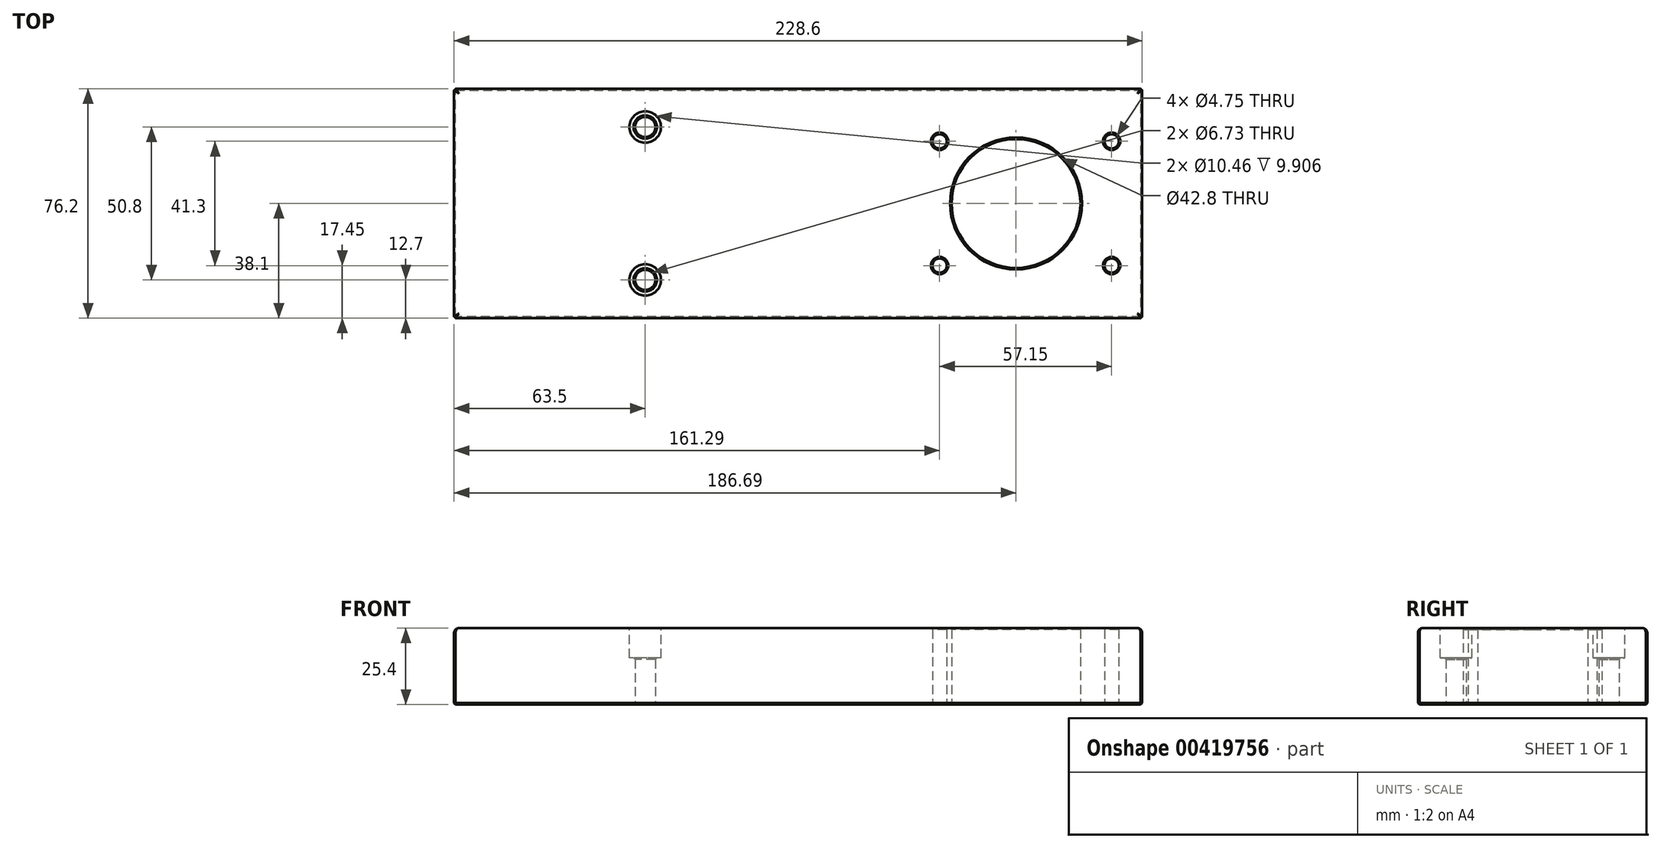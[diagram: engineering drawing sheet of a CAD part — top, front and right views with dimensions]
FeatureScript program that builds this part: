
annotation { "Feature Type Name" : "Feature", "Feature Type Description" : "" }
export const myFeature = defineFeature(function(context is Context, id is Id, definition is map)
    precondition{}
    {
        {
            var Q0;
            Q0=qCreatedBy(makeId("Top.planeOp"),FACE);
            var sketch = newSketch(context, id + "F0", { "sketchPlane" : qUnion([Q0])});
            skLineSegment(sketch, "E0.bottom", {"start": v(-114.3, -38.1) * mm, "end": v(114.3, -38.1) * mm});
            skLineSegment(sketch, "E0.top", {"start": v(-114.3, 38.1) * mm, "end": v(114.3, 38.1) * mm});
            skLineSegment(sketch, "E0.left", {"start": v(-114.3, -38.1) * mm, "end": v(-114.3, 38.1) * mm});
            skLineSegment(sketch, "E0.right", {"start": v(114.3, -38.1) * mm, "end": v(114.3, 38.1) * mm});
            skPoint(sketch, "E0.middle", {"position": v(0, 0) * mm});
            skLineSegment(sketch, "E1", {"start": v(0, 0) * mm, "end": v(0, 0) * mm});
            skPoint(sketch, "E1.endSnap0", {"position": v(0, -38.1) * mm});
            skLineSegment(sketch, "E2", {"start": v(0, 0) * mm, "end": v(-123.94, 0) * mm, "construction": true});
            skLineSegment(sketch, "E3", {"start": v(72.4, 38.1) * mm, "end": v(72.4, -38.1) * mm, "construction": true});
            skCircle(sketch, "E4", {"center": v(72.4, 0) * mm, "radius": 21.4 * mm});
            skCircle(sketch, "E5", {"center": v(104.14, 20.65) * mm, "radius": 2.37 * mm});
            skLineSegment(sketch, "E6", {"start": v(-47.63, 38.1) * mm, "end": v(-47.62, -38.1) * mm, "construction": true});
            skCircle(sketch, "E7", {"center": v(47, 20.65) * mm, "radius": 2.37 * mm});
            skCircle(sketch, "E8.MirrorC", {"center": v(47, -20.65) * mm, "radius": 2.37 * mm});
            skCircle(sketch, "E9.MirrorC", {"center": v(104.14, -20.65) * mm, "radius": 2.37 * mm});
            skLineSegment(sketch, "E10", {"start": v(-102.12, 25.4) * mm, "end": v(-23.36, 25.4) * mm, "construction": true});
            skLineSegment(sketch, "E11.MirrorCS", {"start": v(-102.12, -25.4) * mm, "end": v(-23.36, -25.4) * mm, "construction": true});
            skPoint(sketch, "E12", {"position": v(-47.63, 25.4) * mm});
            skPoint(sketch, "E13", {"position": v(-47.62, -25.4) * mm});
            skSolve(sketch);
        }
        {
            var Q0;
            Q0 = qSketchRegion(id + "F0", true);
            extrude(context, id + "F1", {"entities" : qUnion([Q0]), "depth" : 25.4 * mm});
        }
        {
            var Q0;
            Q0=qCreatedBy(makeId("Top.planeOp"),FACE);
            var sketch = newSketch(context, id + "F2", { "sketchPlane" : qUnion([Q0])});
            skLineSegment(sketch, "E14", {"start": v(-114.74, 25.4) * mm, "end": v(0, 25.4) * mm, "construction": true});
            skLineSegment(sketch, "E15", {"start": v(0, 0) * mm, "end": v(-152.98, 0) * mm, "construction": true});
            skLineSegment(sketch, "E16", {"start": v(-50.8, 25.4) * mm, "end": v(-50.8, 0) * mm, "construction": true});
            skCircle(sketch, "E17", {"center": v(-50.8, 25.4) * mm, "radius": 3.37 * mm});
            skLineSegment(sketch, "E18.MirrorCS", {"start": v(-114.74, -25.4) * mm, "end": v(0, -25.4) * mm, "construction": true});
            skLineSegment(sketch, "E19.MirrorCS", {"start": v(-50.8, -25.4) * mm, "end": v(-50.8, 0) * mm, "construction": true});
            skCircle(sketch, "E20.MirrorC", {"center": v(-50.8, -25.4) * mm, "radius": 3.37 * mm});
            skSolve(sketch);
        }
        {
            var Q0;
            Q0 = qSketchRegion(id + "F2", true);
            extrude(context, id + "F3", {"entities" : qUnion([Q0]), "operationType" : NewBodyOperationType.REMOVE, "depth" : 15.75 * mm});
        }
        {
            var Q0;
            Q0=makeQuery(id+"F1.opExtrude","CAP_FACE",FACE,{"disambiguationData":[OSD([sQuery(id+"F0.wireOp",EDGE,"E0.bottom"),sQuery(id+"F0.wireOp",EDGE,"E0.top"),sQuery(id+"F0.wireOp",EDGE,"E0.left"),sQuery(id+"F0.wireOp",EDGE,"E0.right"),sQuery(id+"F0.wireOp",EDGE,"E4"),sQuery(id+"F0.wireOp",EDGE,"E5"),sQuery(id+"F0.wireOp",EDGE,"E7"),sQuery(id+"F0.wireOp",EDGE,"E8.MirrorC"),sQuery(id+"F0.wireOp",EDGE,"E9.MirrorC")])],"isStart":false});
            var sketch = newSketch(context, id + "F4", { "sketchPlane" : qUnion([Q0])});
            skLineSegment(sketch, "E21", {"start": v(0, 25.4) * mm, "end": v(-89.53, 25.4) * mm, "construction": true});
            skLineSegment(sketch, "E22", {"start": v(0, 0) * mm, "end": v(-84.6, 0) * mm, "construction": true});
            skLineSegment(sketch, "E23", {"start": v(0, -25.4) * mm, "end": v(-84.6, -25.4) * mm, "construction": true});
            skLineSegment(sketch, "E24", {"start": v(-50.8, 25.4) * mm, "end": v(-50.8, -25.4) * mm, "construction": true});
            skCircle(sketch, "E25", {"center": v(-50.8, 25.4) * mm, "radius": 5.23 * mm});
            skCircle(sketch, "E26", {"center": v(-50.8, -25.4) * mm, "radius": 5.23 * mm});
            skSolve(sketch);
        }
        {
            var Q0;
            Q0=makeQuery(id+"F4.imprint","IMPRINT",FACE,{"disambiguationData":[TD([[makeQuery(id+"F4.imprint","IMPRINT",EDGE,{"derivedFrom":sQuery(id+"F4.wireOp",EDGE,"E25")}),1.0]])]});
            var Q1;
            Q1=makeQuery(id+"F4.imprint","IMPRINT",FACE,{"disambiguationData":[TD([[makeQuery(id+"F4.imprint","IMPRINT",EDGE,{"derivedFrom":sQuery(id+"F4.wireOp",EDGE,"E26")}),1.0]])]});
            extrude(context, id + "F5", {"entities" : qUnion([Q0, Q1]), "operationType" : NewBodyOperationType.REMOVE, "oppositeDirection" : true, "depth" : 9.9 * mm});
        }
        {
            var Q0;
            Q0=makeQuery(id+"F1.opExtrude","CAP_EDGE",EDGE,{"disambiguationData":[OSD([sQuery(id+"F0.wireOp",EDGE,"E0.bottom")])],"isStart":false});
            var Q1;
            Q1=makeQuery(id+"F1.opExtrude","CAP_EDGE",EDGE,{"disambiguationData":[OSD([sQuery(id+"F0.wireOp",EDGE,"E0.right")])],"isStart":false});
            var Q2;
            Q2=makeQuery(id+"F1.opExtrude","CAP_EDGE",EDGE,{"disambiguationData":[OSD([sQuery(id+"F0.wireOp",EDGE,"E0.top")])],"isStart":false});
            var Q3;
            Q3=makeQuery(id+"F1.opExtrude","CAP_EDGE",EDGE,{"disambiguationData":[OSD([sQuery(id+"F0.wireOp",EDGE,"E0.left")])],"isStart":false});
            fillet(context, id + "F6", {"entities" : qUnion([Q0, Q1, Q2, Q3]), "radius" : 1.59 * mm, "tangentPropagation" : true, "allowEdgeOverflow" : false});
        }
        {
            var Q0;
            Q0=makeQuery(id+"F1.opExtrude","CAP_EDGE",EDGE,{"disambiguationData":[OSD([sQuery(id+"F0.wireOp",EDGE,"E9.MirrorC")])],"isStart":false});
            var Q1;
            Q1=makeQuery(id+"F1.opExtrude","CAP_EDGE",EDGE,{"disambiguationData":[OSD([sQuery(id+"F0.wireOp",EDGE,"E8.MirrorC")])],"isStart":false});
            var Q2;
            Q2=makeQuery(id+"F1.opExtrude","CAP_EDGE",EDGE,{"disambiguationData":[OSD([sQuery(id+"F0.wireOp",EDGE,"E7")])],"isStart":false});
            var Q3;
            Q3=makeQuery(id+"F1.opExtrude","CAP_EDGE",EDGE,{"disambiguationData":[OSD([sQuery(id+"F0.wireOp",EDGE,"E4")])],"isStart":false});
            var Q4;
            Q4=makeQuery(id+"F1.opExtrude","CAP_EDGE",EDGE,{"disambiguationData":[OSD([sQuery(id+"F0.wireOp",EDGE,"E5")])],"isStart":false});
            var Q5;
            Q5=makeQuery(id+"F1.opExtrude","SWEPT_EDGE",EDGE,{"disambiguationData":[OSD([sQuery(id+"F0.wireOp",EDGE,"E0.top"),sQuery(id+"F0.wireOp",EDGE,"E0.right")])]});
            var Q6;
            Q6=makeQuery(id+"F1.opExtrude","SWEPT_EDGE",EDGE,{"disambiguationData":[OSD([sQuery(id+"F0.wireOp",EDGE,"E0.bottom"),sQuery(id+"F0.wireOp",EDGE,"E0.right")])]});
            var Q7;
            Q7=makeQuery(id+"F5.boolean.opBoolean","COPY",EDGE,{"derivedFrom":makeQuery(id+"F5.opExtrude","CAP_EDGE",EDGE,{"disambiguationData":[OSD([sQuery(id+"F4.wireOp",EDGE,"E26")])],"isStart":true})});
            var Q8;
            Q8=makeQuery(id+"F5.boolean.opBoolean","COPY",EDGE,{"derivedFrom":makeQuery(id+"F5.opExtrude","CAP_EDGE",EDGE,{"disambiguationData":[OSD([sQuery(id+"F4.wireOp",EDGE,"E25")])],"isStart":true})});
            var Q9;
            Q9=makeQuery(id+"F1.opExtrude","SWEPT_EDGE",EDGE,{"disambiguationData":[OSD([sQuery(id+"F0.wireOp",EDGE,"E0.top"),sQuery(id+"F0.wireOp",EDGE,"E0.left")])]});
            var Q10;
            Q10=makeQuery(id+"F1.opExtrude","SWEPT_EDGE",EDGE,{"disambiguationData":[OSD([sQuery(id+"F0.wireOp",EDGE,"E0.bottom"),sQuery(id+"F0.wireOp",EDGE,"E0.left")])]});
            var Q11;
            Q11=makeQuery(id+"F1.opExtrude","CAP_EDGE",EDGE,{"disambiguationData":[OSD([sQuery(id+"F0.wireOp",EDGE,"E7")])],"isStart":true});
            var Q12;
            Q12=makeQuery(id+"F1.opExtrude","CAP_EDGE",EDGE,{"disambiguationData":[OSD([sQuery(id+"F0.wireOp",EDGE,"E4")])],"isStart":true});
            var Q13;
            Q13=makeQuery(id+"F1.opExtrude","CAP_EDGE",EDGE,{"disambiguationData":[OSD([sQuery(id+"F0.wireOp",EDGE,"E8.MirrorC")])],"isStart":true});
            var Q14;
            Q14=makeQuery(id+"F1.opExtrude","CAP_EDGE",EDGE,{"disambiguationData":[OSD([sQuery(id+"F0.wireOp",EDGE,"E5")])],"isStart":true});
            var Q15;
            Q15=makeQuery(id+"F1.opExtrude","CAP_EDGE",EDGE,{"disambiguationData":[OSD([sQuery(id+"F0.wireOp",EDGE,"E9.MirrorC")])],"isStart":true});
            var Q16;
            Q16=makeQuery(id+"F1.opExtrude","CAP_EDGE",EDGE,{"disambiguationData":[OSD([sQuery(id+"F0.wireOp",EDGE,"E0.right")])],"isStart":true});
            var Q17;
            Q17=makeQuery(id+"F1.opExtrude","CAP_EDGE",EDGE,{"disambiguationData":[OSD([sQuery(id+"F0.wireOp",EDGE,"E0.bottom")])],"isStart":true});
            var Q18;
            Q18=makeQuery(id+"F1.opExtrude","CAP_EDGE",EDGE,{"disambiguationData":[OSD([sQuery(id+"F0.wireOp",EDGE,"E0.top")])],"isStart":true});
            var Q19;
            Q19=makeQuery(id+"F3.boolean.opBoolean","COPY",EDGE,{"derivedFrom":makeQuery(id+"F3.opExtrude","CAP_EDGE",EDGE,{"disambiguationData":[OSD([sQuery(id+"F2.wireOp",EDGE,"E20.MirrorC")])],"isStart":true})});
            var Q20;
            Q20=makeQuery(id+"F3.boolean.opBoolean","COPY",EDGE,{"derivedFrom":makeQuery(id+"F3.opExtrude","CAP_EDGE",EDGE,{"disambiguationData":[OSD([sQuery(id+"F2.wireOp",EDGE,"E17")])],"isStart":true})});
            var Q21;
            Q21=makeQuery(id+"F1.opExtrude","CAP_FACE",FACE,{"disambiguationData":[OSD([sQuery(id+"F0.wireOp",EDGE,"E0.bottom"),sQuery(id+"F0.wireOp",EDGE,"E0.top"),sQuery(id+"F0.wireOp",EDGE,"E0.left"),sQuery(id+"F0.wireOp",EDGE,"E0.right"),sQuery(id+"F0.wireOp",EDGE,"E4"),sQuery(id+"F0.wireOp",EDGE,"E5"),sQuery(id+"F0.wireOp",EDGE,"E7"),sQuery(id+"F0.wireOp",EDGE,"E8.MirrorC"),sQuery(id+"F0.wireOp",EDGE,"E9.MirrorC")])],"isStart":true});
            var Q22;
            Q22=makeQuery(id+"F5.boolean.opBoolean","INTERSECT",EDGE,{"derivedFrom":[makeQuery(id+"F3.boolean.opBoolean","COPY",FACE,{"derivedFrom":makeQuery(id+"F3.opExtrude","SWEPT_FACE",FACE,{"disambiguationData":[OSD([sQuery(id+"F2.wireOp",EDGE,"E17")])]})}),makeQuery(id+"F5.opExtrude","CAP_FACE",FACE,{"disambiguationData":[OSD([sQuery(id+"F4.wireOp",EDGE,"E25")])],"isStart":false})]});
            var Q23;
            Q23=makeQuery(id+"F5.boolean.opBoolean","INTERSECT",EDGE,{"derivedFrom":[makeQuery(id+"F3.boolean.opBoolean","COPY",FACE,{"derivedFrom":makeQuery(id+"F3.opExtrude","SWEPT_FACE",FACE,{"disambiguationData":[OSD([sQuery(id+"F2.wireOp",EDGE,"E20.MirrorC")])]})}),makeQuery(id+"F5.opExtrude","CAP_FACE",FACE,{"disambiguationData":[OSD([sQuery(id+"F4.wireOp",EDGE,"E26")])],"isStart":false})]});
            chamfer(context, id + "F7", {"entities" : qUnion([Q0, Q1, Q2, Q3, Q4, Q5, Q6, Q7, Q8, Q9, Q10, Q11, Q12, Q13, Q14, Q15, Q16, Q17, Q18, Q19, Q20, Q21, Q22, Q23]), "width" : 0.5 * mm, "tangentPropagation" : true});
        }
    });
